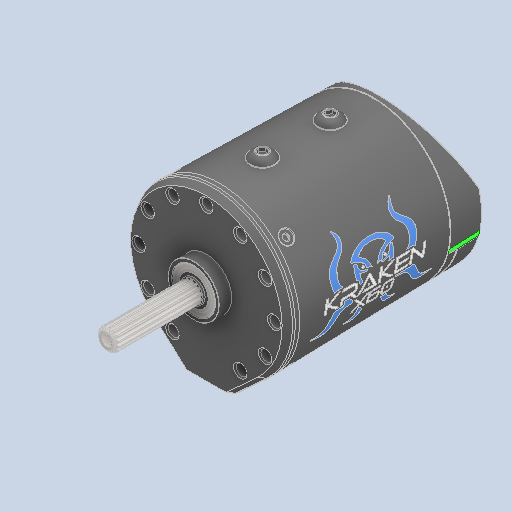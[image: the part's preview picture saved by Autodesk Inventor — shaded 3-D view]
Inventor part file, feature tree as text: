
AUTODESK INVENTOR PART (.ipt)
format: ipt  version: 2024 (Build 280153000, 153)  size: 8,707,072 bytes
history: native  units: in
note: dims shown in document units (in); Inventor stores cm internally (conversion verified against a paired STEP export)
features: other x5, mirror x1
ambient origin geometry x8: Origin, YZ Plane, XZ Plane, XY Plane, X Axis, Y Axis, Z Axis, Center Point
bodies: Solid1 (feature_tree), Solid2 (feature_tree), Solid3 (feature_tree), Solid4 (feature_tree), Solid5 (feature_tree), Solid6 (feature_tree)
feature tree (6):
  parser-record x1  (decoder bookkeeping rows leaked as tree rows — omitted from the tree; the rows remain in map.json)
  other  "NONE:1"
  other  "WCP-0940-204 Rev3"
  other  "NONE:2"
  other  "STB0440"
  mirror  "Mirror1"
